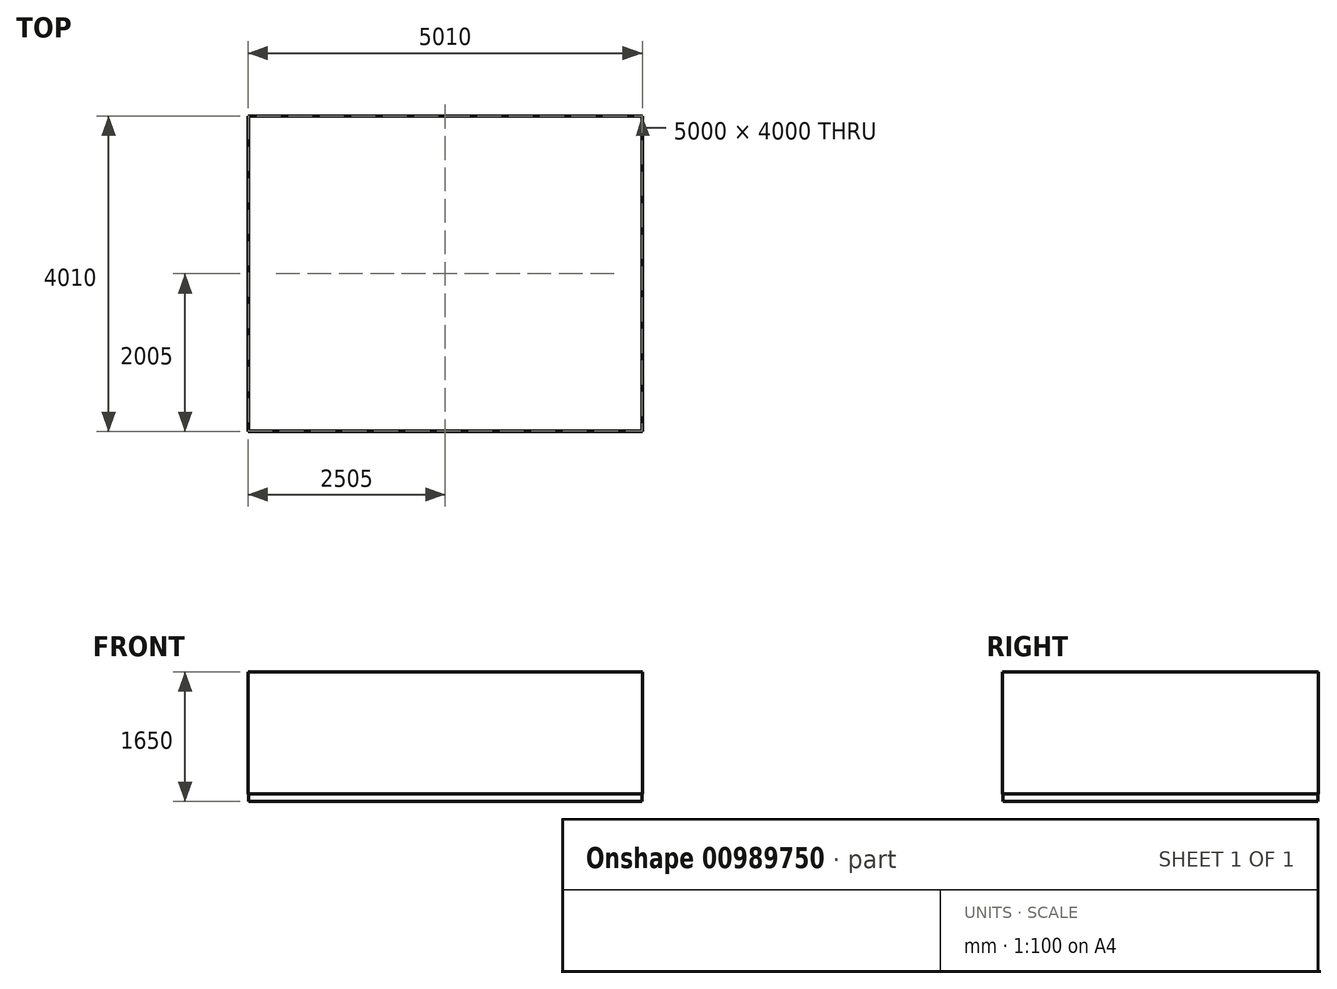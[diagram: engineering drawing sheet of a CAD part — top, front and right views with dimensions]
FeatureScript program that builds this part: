
annotation { "Feature Type Name" : "Feature", "Feature Type Description" : "" }
export const myFeature = defineFeature(function(context is Context, id is Id, definition is map)
    precondition{}
    {
        {
            var Q0;
            Q0=qCreatedBy(makeId("Top.planeOp"),FACE);
            var sketch = newSketch(context, id + "F0", { "sketchPlane" : qUnion([Q0])});
            skLineSegment(sketch, "E0.bottom", {"start": v(2500, -2000) * mm, "end": v(-2500, -2000) * mm});
            skLineSegment(sketch, "E0.top", {"start": v(2500, 2000) * mm, "end": v(-2500, 2000) * mm});
            skLineSegment(sketch, "E0.left", {"start": v(2500, -2000) * mm, "end": v(2500, 2000) * mm});
            skLineSegment(sketch, "E0.right", {"start": v(-2500, -2000) * mm, "end": v(-2500, 2000) * mm});
            skPoint(sketch, "E0.middle", {"position": v(0, 0) * mm});
            skSolve(sketch);
        }
        {
            var Q0;
            Q0 = qSketchRegion(id + "F0", true);
            extrude(context, id + "F1", {"entities" : qUnion([Q0]), "depth" : 100 * mm, "offsetDistance" : 25 * mm});
        }
        {
            var Q0;
            Q0=makeQuery(id+"F1.opExtrude","CAP_FACE",FACE,{"disambiguationData":[OSD([sQuery(id+"F0.wireOp",EDGE,"E0.bottom"),sQuery(id+"F0.wireOp",EDGE,"E0.top"),sQuery(id+"F0.wireOp",EDGE,"E0.left"),sQuery(id+"F0.wireOp",EDGE,"E0.right")])],"isStart":false});
            var sketch = newSketch(context, id + "F2", { "sketchPlane" : qUnion([Q0])});
            skLineSegment(sketch, "E1.bottom", {"start": v(2500, -2000) * mm, "end": v(-2500, -2000) * mm});
            skLineSegment(sketch, "E1.top", {"start": v(2500, 2000) * mm, "end": v(-2500, 2000) * mm});
            skLineSegment(sketch, "E1.left", {"start": v(2500, -2000) * mm, "end": v(2500, 2000) * mm});
            skLineSegment(sketch, "E1.right", {"start": v(-2500, -2000) * mm, "end": v(-2500, 2000) * mm});
            skPoint(sketch, "E1.middle", {"position": v(0, 0) * mm});
            skLineSegment(sketch, "E2.0", {"start": v(2400, 1900) * mm, "end": v(100, 1900) * mm});
            skLineSegment(sketch, "E2.1", {"start": v(2400, -1900) * mm, "end": v(2400, -100) * mm});
            skLineSegment(sketch, "E2.2", {"start": v(2400, -1900) * mm, "end": v(0, -1900) * mm});
            skLineSegment(sketch, "E2.3", {"start": v(-2400, -1900) * mm, "end": v(-2400, 0) * mm});
            skLineSegment(sketch, "E3.bottom", {"start": v(1500, -1000) * mm, "end": v(0, -1000) * mm});
            skLineSegment(sketch, "E3.top", {"start": v(1500, 1000) * mm, "end": v(100, 1000) * mm});
            skLineSegment(sketch, "E3.left", {"start": v(1500, -1000) * mm, "end": v(1500, -100) * mm});
            skLineSegment(sketch, "E3.right", {"start": v(-1500, -1000) * mm, "end": v(-1500, 0) * mm});
            skLineSegment(sketch, "E4.0", {"start": v(1400, 900) * mm, "end": v(-1400, 900) * mm});
            skLineSegment(sketch, "E4.1", {"start": v(1400, -900) * mm, "end": v(1400, 900) * mm});
            skLineSegment(sketch, "E4.2", {"start": v(1400, -900) * mm, "end": v(-1400, -900) * mm});
            skLineSegment(sketch, "E4.3", {"start": v(-1400, -900) * mm, "end": v(-1400, 900) * mm});
            skLineSegment(sketch, "E5", {"start": v(-1500, 0) * mm, "end": v(-2400, 0) * mm});
            skLineSegment(sketch, "E6", {"start": v(0, 1000) * mm, "end": v(0, 1900) * mm});
            skLineSegment(sketch, "E7", {"start": v(1500, 0) * mm, "end": v(2400, 0) * mm});
            skLineSegment(sketch, "E8", {"start": v(0, -1000) * mm, "end": v(0, -1900) * mm});
            skLineSegment(sketch, "E9.0", {"start": v(-1500, 100) * mm, "end": v(-2400, 100) * mm});
            skLineSegment(sketch, "E10.0", {"start": v(100, 1000) * mm, "end": v(100, 1900) * mm});
            skLineSegment(sketch, "E11.0", {"start": v(1500, -100) * mm, "end": v(2400, -100) * mm});
            skLineSegment(sketch, "E12.0", {"start": v(2505, -2005) * mm, "end": v(2505, 2005) * mm});
            skLineSegment(sketch, "E12.1", {"start": v(-2505, -2005) * mm, "end": v(2505, -2005) * mm});
            skLineSegment(sketch, "E12.2", {"start": v(-2505, 2005) * mm, "end": v(-2505, -2005) * mm});
            skLineSegment(sketch, "E12.3", {"start": v(2505, 2005) * mm, "end": v(-2505, 2005) * mm});
            skLineSegment(sketch, "E13.0", {"start": v(-100, -1000) * mm, "end": v(-100, -1900) * mm});
            skLineSegment(sketch, "E14.trimOffspring", {"start": v(0, 1000) * mm, "end": v(-1500, 1000) * mm});
            skLineSegment(sketch, "E15.trimOffspring", {"start": v(1500, 0) * mm, "end": v(1500, 1000) * mm});
            skLineSegment(sketch, "E16.trimOffspring", {"start": v(2400, 0) * mm, "end": v(2400, 1900) * mm});
            skLineSegment(sketch, "E17.trimOffspring", {"start": v(0, 1900) * mm, "end": v(-2400, 1900) * mm});
            skLineSegment(sketch, "E18.trimOffspring", {"start": v(-1500, 100) * mm, "end": v(-1500, 1000) * mm});
            skLineSegment(sketch, "E19.trimOffspring", {"start": v(-2400, 100) * mm, "end": v(-2400, 1900) * mm});
            skLineSegment(sketch, "E20.trimOffspring", {"start": v(-100, -1000) * mm, "end": v(-1500, -1000) * mm});
            skLineSegment(sketch, "E21.trimOffspring", {"start": v(-100, -1900) * mm, "end": v(-2400, -1900) * mm});
            skSolve(sketch);
        }
        {
            var Q0;
            Q0 = qSketchRegion(id + "F2", true);
            extrude(context, id + "F3", {"entities" : qUnion([Q0]), "depth" : 1550 * mm, "offsetDistance" : 25 * mm});
        }
    });
